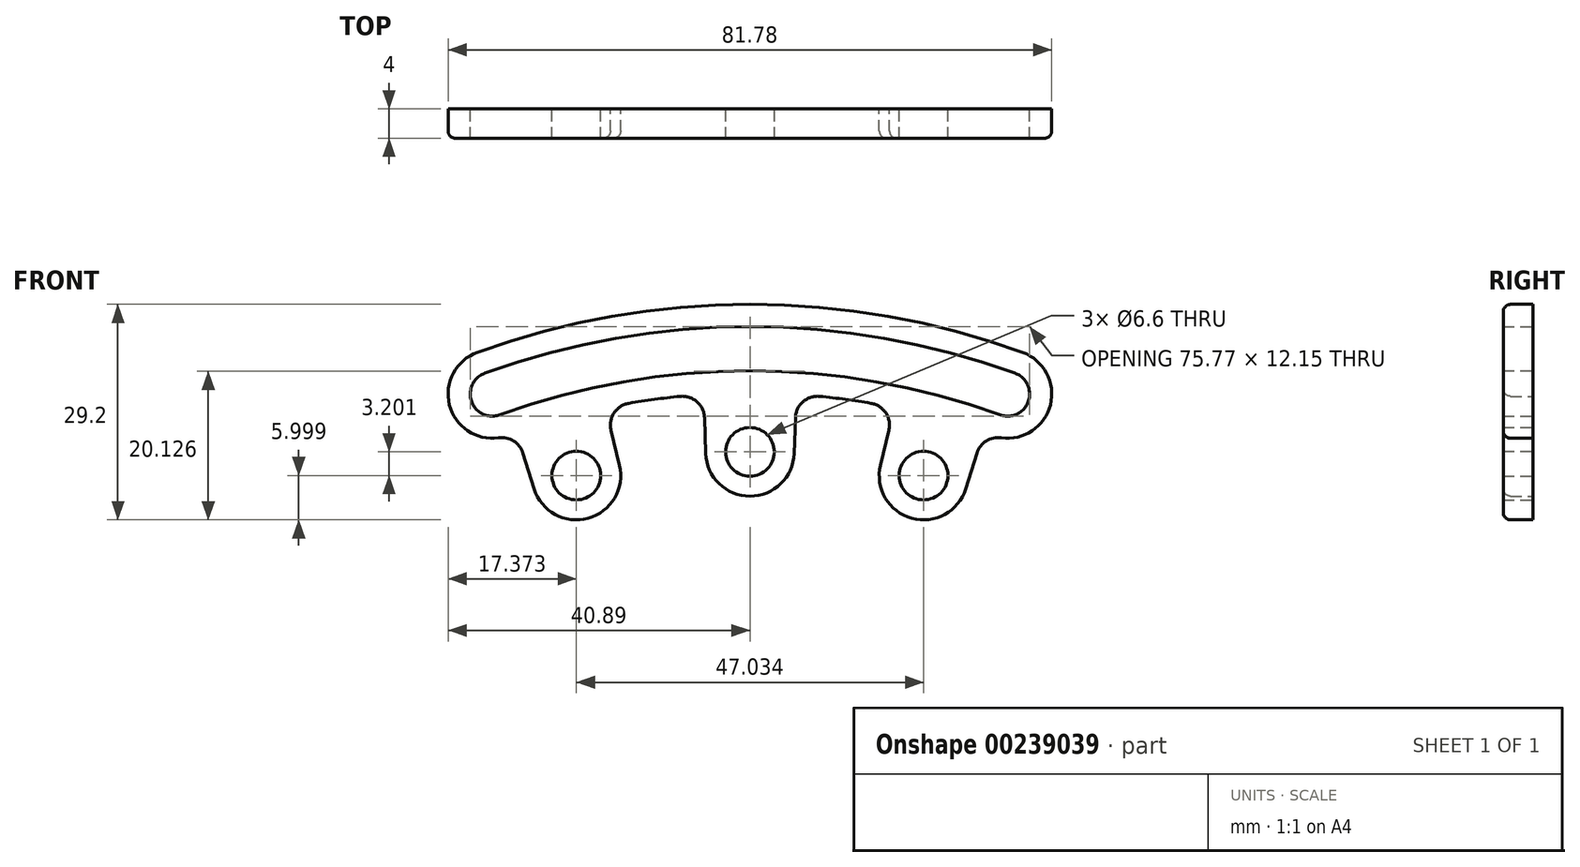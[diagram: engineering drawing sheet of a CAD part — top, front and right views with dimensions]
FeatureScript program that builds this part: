
annotation { "Feature Type Name" : "Feature", "Feature Type Description" : "" }
export const myFeature = defineFeature(function(context is Context, id is Id, definition is map)
    precondition{}
    {
        {
            var Q0;
            Q0=qCreatedBy(makeId("Front.planeOp"),FACE);
            var sketch = newSketch(context, id + "F0", { "sketchPlane" : qUnion([Q0])});
            skLineSegment(sketch, "E0", {"start": v(0, 0) * mm, "end": v(32.83, 90.21) * mm, "construction": true});
            skLineSegment(sketch, "E1", {"start": v(0, 0) * mm, "end": v(-32.83, 90.21) * mm, "construction": true});
            skArc(sketch, "E2", {"start": v(36.94, 101.49) * mm, "mid": v(0, 108) * mm, "end": v(-36.94, 101.49) * mm});
            skArc(sketch, "E3", {"start": v(35.91, 98.67) * mm, "mid": v(0, 105) * mm, "end": v(-35.91, 98.67) * mm});
            skArc(sketch, "E4", {"start": v(33.86, 93.03) * mm, "mid": v(0, 99) * mm, "end": v(-33.86, 93.03) * mm});
            skArc(sketch, "E5", {"start": v(-35.91, 98.67) * mm, "mid": v(-37.7, 94.82) * mm, "end": v(-33.86, 93.03) * mm});
            skArc(sketch, "E6", {"start": v(33.86, 93.03) * mm, "mid": v(37.7, 94.82) * mm, "end": v(35.91, 98.67) * mm});
            skPoint(sketch, "E7.orphan", {"position": v(0, 108) * mm});
            skArc(sketch, "E8", {"start": v(-29.24, 83) * mm, "mid": v(-21.91, 79.02) * mm, "end": v(-17.68, 86.2) * mm});
            skArc(sketch, "E9", {"start": v(-6, 87.8) * mm, "mid": v(0, 82) * mm, "end": v(6, 87.8) * mm});
            skArc(sketch, "E10", {"start": v(17.68, 86.2) * mm, "mid": v(21.91, 79.02) * mm, "end": v(29.24, 83) * mm});
            skArc(sketch, "E11", {"start": v(-36.94, 101.49) * mm, "mid": v(-40.7, 94.4) * mm, "end": v(-34.04, 89.9) * mm});
            skArc(sketch, "E12", {"start": v(34.04, 89.9) * mm, "mid": v(40.7, 94.4) * mm, "end": v(36.94, 101.49) * mm});
            skArc(sketch, "E13", {"start": v(-9.46, 95.53) * mm, "mid": v(-12.95, 95.12) * mm, "end": v(-16.42, 94.59) * mm});
            skCircle(sketch, "E14", {"center": v(-23.52, 84.8) * mm, "radius": 3.3 * mm});
            skCircle(sketch, "E15", {"center": v(0, 88) * mm, "radius": 3.3 * mm});
            skCircle(sketch, "E16", {"center": v(23.52, 84.8) * mm, "radius": 3.3 * mm});
            skLineSegment(sketch, "E17", {"start": v(-29.24, 83) * mm, "end": v(-30.76, 87.84) * mm});
            skLineSegment(sketch, "E18", {"start": v(29.24, 83) * mm, "end": v(30.76, 87.84) * mm});
            skLineSegment(sketch, "E19", {"start": v(-17.68, 86.2) * mm, "end": v(-18.82, 90.93) * mm});
            skLineSegment(sketch, "E20", {"start": v(17.68, 86.2) * mm, "end": v(18.82, 90.93) * mm});
            skLineSegment(sketch, "E21", {"start": v(-6, 87.8) * mm, "end": v(-6.16, 92.65) * mm});
            skLineSegment(sketch, "E22", {"start": v(6, 87.8) * mm, "end": v(6.16, 92.65) * mm});
            skArc(sketch, "E23.filletArc", {"start": v(-30.76, 87.84) * mm, "mid": v(-32.02, 89.48) * mm, "end": v(-34.04, 89.9) * mm});
            skArc(sketch, "E24.filletArc", {"start": v(34.04, 89.9) * mm, "mid": v(32.02, 89.48) * mm, "end": v(30.76, 87.84) * mm});
            skArc(sketch, "E25.filletArc", {"start": v(18.82, 90.93) * mm, "mid": v(18.41, 93.28) * mm, "end": v(16.42, 94.59) * mm});
            skArc(sketch, "E26.filletArc", {"start": v(-16.42, 94.59) * mm, "mid": v(-18.41, 93.28) * mm, "end": v(-18.82, 90.93) * mm});
            skArc(sketch, "E27.MirrorCS", {"start": v(9.46, 95.53) * mm, "mid": v(12.95, 95.12) * mm, "end": v(16.42, 94.59) * mm});
            skPoint(sketch, "E28.newPointB", {"position": v(16.42, 94.59) * mm});
            skArc(sketch, "E28.filletArc", {"start": v(-6.16, 92.65) * mm, "mid": v(-7.18, 94.8) * mm, "end": v(-9.46, 95.53) * mm});
            skPoint(sketch, "E29.newPointB", {"position": v(-16.42, 94.59) * mm});
            skArc(sketch, "E29.filletArc", {"start": v(9.46, 95.53) * mm, "mid": v(7.18, 94.8) * mm, "end": v(6.16, 92.65) * mm});
            skSolve(sketch);
        }
        {
            var Q0;
            Q0=makeQuery(id+"F0.imprint","IMPRINT",FACE,{"disambiguationData":[TD([[makeQuery(id+"F0.imprint","IMPRINT",EDGE,{"derivedFrom":sQuery(id+"F0.wireOp",EDGE,"E2")}),1.0]])]});
            extrude(context, id + "F1", {"entities" : qUnion([Q0]), "depth" : 4 * mm});
        }
        {
            var Q0;
            Q0=makeQuery(id+"F1.opExtrude","CAP_EDGE",EDGE,{"disambiguationData":[OSD([sQuery(id+"F0.wireOp",EDGE,"E2")])],"isStart":false});
            fillet(context, id + "F2", {"entities" : qUnion([Q0]), "radius" : 1 * mm, "tangentPropagation" : true, "allowEdgeOverflow" : false});
        }
    });
